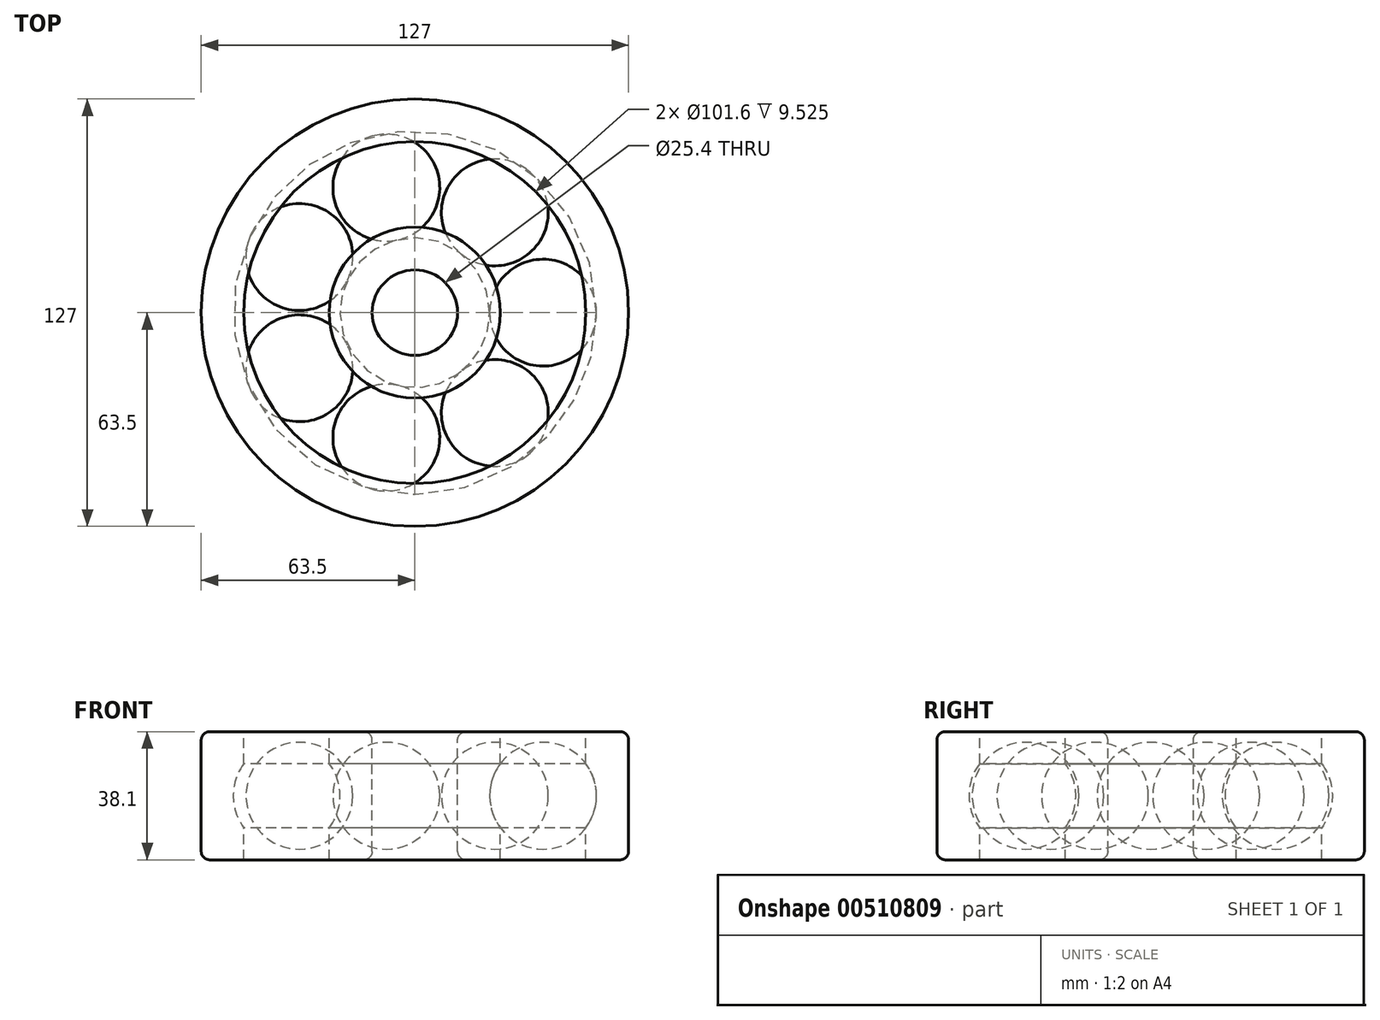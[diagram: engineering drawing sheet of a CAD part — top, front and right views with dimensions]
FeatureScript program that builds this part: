
annotation { "Feature Type Name" : "Feature", "Feature Type Description" : "" }
export const myFeature = defineFeature(function(context is Context, id is Id, definition is map)
    precondition{}
    {
        {
            var Q0;
            Q0=qCreatedBy(makeId("Front.planeOp"),FACE);
            var sketch = newSketch(context, id + "F0", { "sketchPlane" : qUnion([Q0])});
            skLineSegment(sketch, "E0", {"start": v(0, 19.05) * mm, "end": v(0, -19.05) * mm, "construction": true});
            skLineSegment(sketch, "E1", {"start": v(12.7, 19.05) * mm, "end": v(12.7, -19.05) * mm});
            skLineSegment(sketch, "E2", {"start": v(12.7, -19.05) * mm, "end": v(25.4, -19.05) * mm});
            skLineSegment(sketch, "E3", {"start": v(25.4, -19.05) * mm, "end": v(25.4, 19.05) * mm});
            skLineSegment(sketch, "E4", {"start": v(25.4, 19.05) * mm, "end": v(12.7, 19.05) * mm});
            skCircle(sketch, "E5", {"center": v(38.1, 0) * mm, "radius": 15.88 * mm});
            skLineSegment(sketch, "E6.bottom", {"start": v(50.8, 19.05) * mm, "end": v(63.5, 19.05) * mm});
            skLineSegment(sketch, "E6.top", {"start": v(50.8, -19.05) * mm, "end": v(63.5, -19.05) * mm});
            skLineSegment(sketch, "E6.left", {"start": v(50.8, 19.05) * mm, "end": v(50.8, -19.05) * mm});
            skLineSegment(sketch, "E6.right", {"start": v(63.5, 19.05) * mm, "end": v(63.5, -19.05) * mm});
            skLineSegment(sketch, "E7", {"start": v(22.22, 0) * mm, "end": v(53.97, 0) * mm});
            skLineSegment(sketch, "E8", {"start": v(12.7, 0) * mm, "end": v(22.22, 0) * mm, "construction": true});
            skLineSegment(sketch, "E9", {"start": v(53.97, 0) * mm, "end": v(63.5, 0) * mm, "construction": true});
            skSolve(sketch);
        }
        {
            var Q0;
            Q0=makeQuery(id+"F0.imprint","IMPRINT",FACE,{"disambiguationData":[TD([[makeQuery(id+"F0.imprint","IMPRINT",EDGE,{"derivedFrom":sQuery(id+"F0.wireOp",EDGE,"E1")}),1.0]])]});
            var Q1;
            {var subQ1=sQuery(id+"F0.wireOp",EDGE,"E6.bottom");Q1=makeQuery(id+"F0.imprint","IMPRINT",FACE,{"disambiguationData":[TD([[makeQuery(id+"F0.imprint","IMPRINT",EDGE,{"derivedFrom":subQ1}),-1.0]])]});}
            var Q2;
            Q2=sQuery(id+"F0.wireOp",EDGE,"E0");
            revolve(context, id + "F1", {"entities" : qUnion([Q0, Q1]), "axis" : qUnion([Q2]), "revolveType" : RevolveType.FULL});
        }
        {
            var Q0;
            {var subQ0=sQuery(id+"F0.wireOp",EDGE,"E5");var subQ1=sQuery(id+"F0.wireOp",EDGE,"E3");var subQ2=makeQuery(id+"F0.imprint","INTERSECT",VERTEX,{"disambiguationData":[OD(1.0)],"derivedFrom":[subQ1,subQ0]});Q0=makeQuery(id+"F0.imprint","IMPRINT",FACE,{"disambiguationData":[TD([[makeQuery(id+"F0.imprint","IMPRINT",EDGE,{"disambiguationData":[TD([[subQ2,1.0]])],"derivedFrom":subQ1}),1.0]])]});}
            var Q1;
            {var subQ0=sQuery(id+"F0.wireOp",EDGE,"E5");var subQ1=sQuery(id+"F0.wireOp",EDGE,"E3");var subQ2=makeQuery(id+"F0.imprint","INTERSECT",VERTEX,{"disambiguationData":[OD(1.0)],"derivedFrom":[subQ1,subQ0]});Q1=makeQuery(id+"F0.imprint","IMPRINT",FACE,{"disambiguationData":[TD([[makeQuery(id+"F0.imprint","IMPRINT",EDGE,{"disambiguationData":[TD([[subQ2,1.0]])],"derivedFrom":subQ1}),-1.0]])]});}
            var Q2;
            {var subQ0=sQuery(id+"F0.wireOp",EDGE,"E7");var subQ1=sQuery(id+"F0.wireOp",EDGE,"E5");var subQ2=makeQuery(id+"F0.imprint","INTERSECT",VERTEX,{"disambiguationData":[OD(1.0)],"derivedFrom":[subQ1,subQ0]});Q2=makeQuery(id+"F0.imprint","IMPRINT",FACE,{"disambiguationData":[TD([[makeQuery(id+"F0.imprint","IMPRINT",EDGE,{"disambiguationData":[TD([[subQ2,-1.0]])],"derivedFrom":subQ1}),1.0]])]});}
            var Q3;
            Q3=sQuery(id+"F0.wireOp",EDGE,"E7");
            revolve(context, id + "F2", {"entities" : qUnion([Q0, Q1, Q2]), "axis" : qUnion([Q3]), "revolveType" : RevolveType.FULL});
        }
        {
            var Q0;
            Q0=makeQuery(id+"F2.opRevolve","SWEPT_BODY",BODY,{"disambiguationData":[OSD([sQuery(id+"F0.wireOp",EDGE,"E5"),sQuery(id+"F0.wireOp",EDGE,"E7")])]});
            var Q1;
            Q1=sQuery(id+"F0.wireOp",EDGE,"E0");
            circularPattern(context, id + "F3", {"entities" : qUnion([Q0]), "axis" : qUnion([Q1]), "angle" : 360 * degree, "instanceCount" : 7, "equalSpace" : true});
        }
        {
            var Q0;
            Q0=makeQuery(id+"F1.opRevolve","SWEPT_EDGE",EDGE,{"disambiguationData":[OSD([sQuery(id+"F0.wireOp",EDGE,"E6.bottom"),sQuery(id+"F0.wireOp",EDGE,"E6.right")])]});
            var Q1;
            Q1=makeQuery(id+"F1.opRevolve","SWEPT_EDGE",EDGE,{"disambiguationData":[OSD([sQuery(id+"F0.wireOp",EDGE,"E6.top"),sQuery(id+"F0.wireOp",EDGE,"E6.right")])]});
            var Q2;
            Q2=makeQuery(id+"F1.opRevolve","SWEPT_EDGE",EDGE,{"disambiguationData":[OSD([sQuery(id+"F0.wireOp",EDGE,"E1"),sQuery(id+"F0.wireOp",EDGE,"E2")])]});
            var Q3;
            Q3=makeQuery(id+"F1.opRevolve","SWEPT_EDGE",EDGE,{"disambiguationData":[OSD([sQuery(id+"F0.wireOp",EDGE,"E1"),sQuery(id+"F0.wireOp",EDGE,"E4")])]});
            fillet(context, id + "F4", {"entities" : qUnion([Q0, Q1, Q2, Q3]), "radius" : 2.54 * mm, "tangentPropagation" : true, "allowEdgeOverflow" : false});
        }
    });
